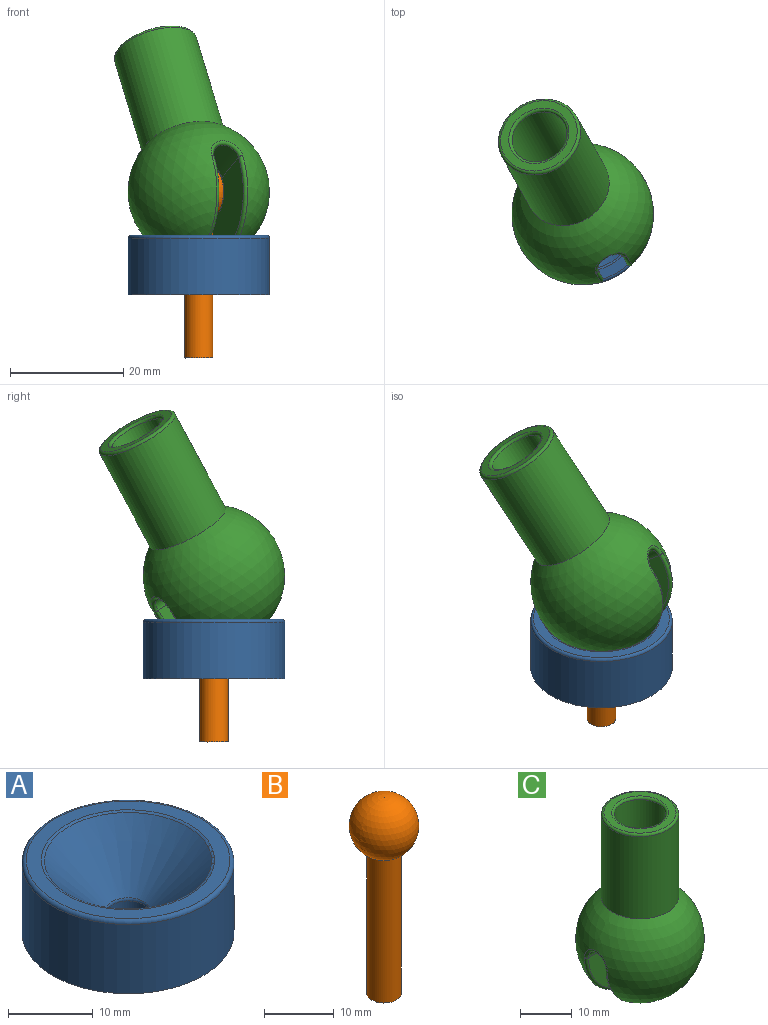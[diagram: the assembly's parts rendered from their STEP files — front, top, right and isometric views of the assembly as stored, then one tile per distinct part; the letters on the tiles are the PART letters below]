
ASSEMBLY  parts=3 mates=2
PART A: 9 faces, bbox 27.1x27.1x10.5 mm
  f0: plane 24x24mm, normal (0,0,1), area 125.1mm2, adj f5,f8
  f1: cone r=2.5mm half-angle=45deg, axis (0,0,1), area 400.3mm2, adj f5,f6
  f2: cylinder r=2.5mm len=5mm, axis (0,0,1), area 36mm2, adj f6,f7
  f3: plane 25x25mm, normal (0,0,-1), area 462.6mm2, adj f4,f7
  f4: cylinder r=12.5mm len=25mm, axis (0,0,1), area 785.4mm2, adj f3,f8
  f5: torus R=10.21mm, axis (0,0,1), area 24.7mm2, adj f0,f1
  f6: torus R=3mm, axis (0,0,-1), area 6.3mm2, adj f1,f2
  f7: torus R=3mm, axis (0,0,1), area 13.2mm2, adj f2,f3
  f8: torus R=12mm, axis (0,0,1), area 60.8mm2, adj f0,f4
PART B: 3 faces, bbox 10x10x34.3 mm
  f0: cylinder r=2.5mm len=25mm, axis (0,0,-1), area 392.7mm2, adj f1,f2
  f1: sphere r=5mm, area 293.1mm2, adj f0
  f2: plane 5x5mm, normal (0,0,-1), area 19.6mm2, adj f0
PART C: 20 faces, bbox 26.2x25x43.1 mm
  f0: sphere r=5mm, area 35.7mm2, adj f5,f13
  f1: sphere r=12.5mm, area 1490.5mm2, adj f3,f14,f15,f16,f17
  f2: sphere r=5mm, area 35.7mm2, adj f5,f10
  f3: cylinder r=7.5mm len=19.5mm, axis (0,0,-1), area 918.9mm2, adj f1,f18
  f4: plane 14x14mm, normal (0,0,1), area 58.9mm2, adj f18,f19
  f5: cylinder r=5mm len=29.5mm, axis (0,0,-1), area 900mm2, adj f0,f2,f11,f12,f19
  f6: plane 23.24x11.62mm, normal (0,-1,0), area 178.7mm2, adj f8,f9,f13,f14
  f7: plane 23.24x11.62mm, normal (0,1,0), area 178.7mm2, adj f8,f9,f10,f17
  f8: cylinder r=2.5mm len=7.01mm, axis (1,0,0), area 51.5mm2, adj f6,f7,f11,f15
  f9: cylinder r=2.5mm len=7.01mm, axis (1,0,0), area 51.5mm2, adj f6,f7,f12,f16
  f10: torus R=4.61mm, axis (0,-1,0), area 6.8mm2, adj f2,f7,f11,f12
  f11: bspline ~5.46x3.51mm, area 5.4mm2, adj f5,f8,f10,f13
  f12: bspline ~5.46x3.51mm, area 5.4mm2, adj f5,f9,f10,f13
  f13: torus R=4.61mm, axis (0,-1,0), area 6.8mm2, adj f0,f6,f11,f12
  f14: torus R=11.62mm, axis (0,-1,0), area 34.3mm2, adj f1,f6,f15,f16
  f15: torus R=3mm, axis (-1,0,0), area 7.8mm2, adj f1,f8,f14,f17
  f16: torus R=3mm, axis (1,0,0), area 7.8mm2, adj f1,f9,f14,f17
  f17: torus R=11.62mm, axis (0,-1,0), area 34.3mm2, adj f1,f7,f15,f16
  f18: torus R=7mm, axis (0,0,-1), area 36.1mm2, adj f3,f4
  f19: torus R=5.5mm, axis (0,0,-1), area 25.6mm2, adj f4,f5
PLACE A t=(-0.62,-0.97,1.61)mm fixed
PLACE B rot(axis=(0,0,1),101.3deg) t=(-0.62,-0.97,-9.54)mm
PLACE C rot(axis=(-0.25,-0.42,-0.87),67.7deg) t=(2.6,-6.7,9.15)mm
MATE ball B.f0 <-> C.f3  axis (0,0,1) through (-0.62,-0.97,19.79)mm
MATE cylindrical B.f0 <-> A.f1  axis (0,0,-1) through (-0.62,-0.97,2.96)mm
